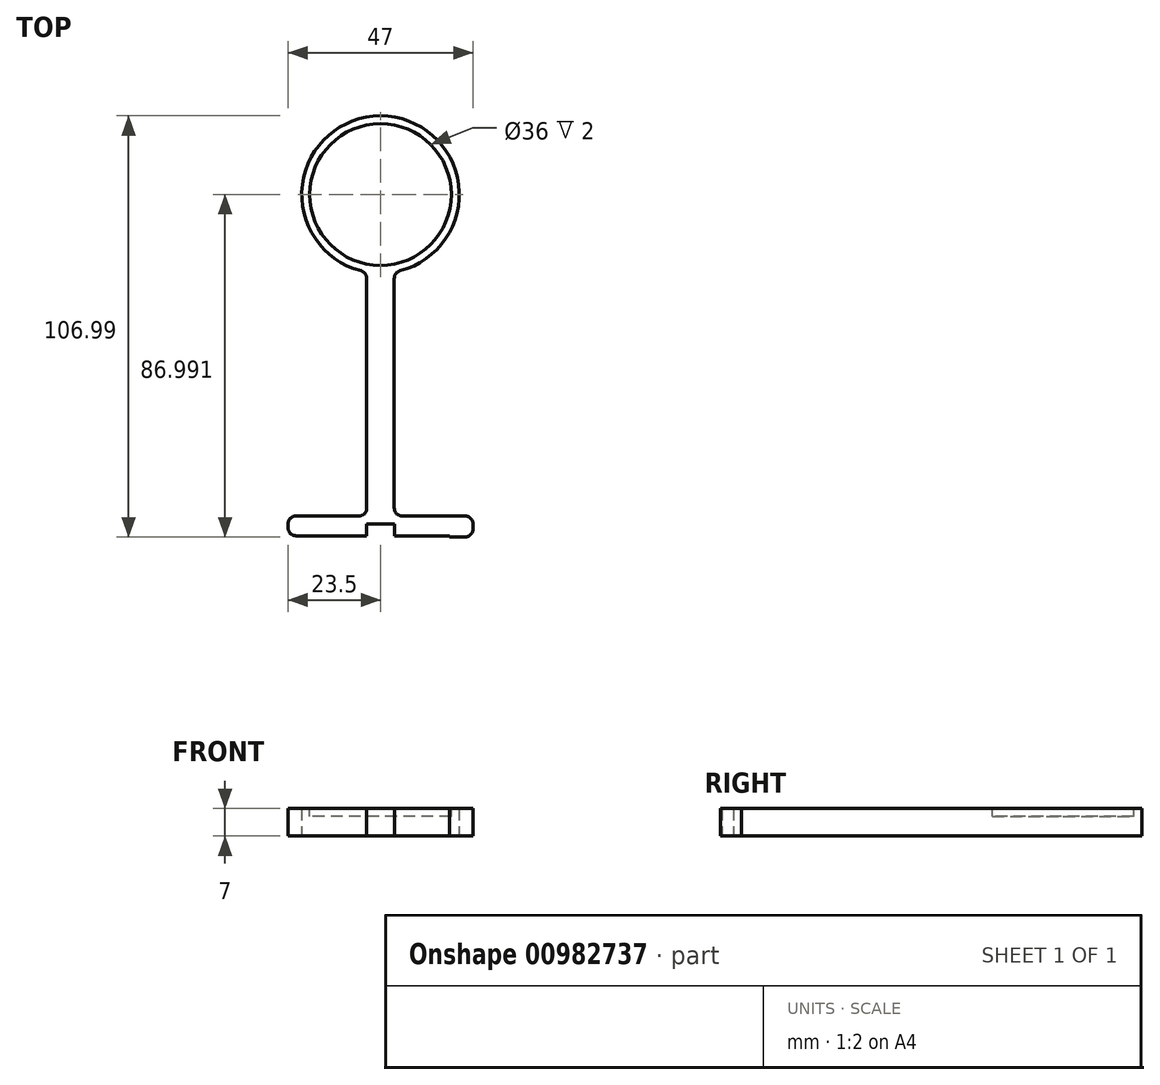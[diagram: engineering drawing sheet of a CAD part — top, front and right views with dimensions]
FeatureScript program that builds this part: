
annotation { "Feature Type Name" : "Feature", "Feature Type Description" : "" }
export const myFeature = defineFeature(function(context is Context, id is Id, definition is map)
    precondition{}
    {
        {
            var Q0;
            Q0=qCreatedBy(makeId("Top.planeOp"),FACE);
            var sketch = newSketch(context, id + "F0", { "sketchPlane" : qUnion([Q0])});
            skLineSegment(sketch, "E0", {"start": v(-3.5, -3) * mm, "end": v(-3.5, -65) * mm});
            skLineSegment(sketch, "E1", {"start": v(-3.5, -65) * mm, "end": v(-23.5, -65) * mm});
            skLineSegment(sketch, "E2", {"start": v(-23.5, -65) * mm, "end": v(-23.5, -70) * mm});
            skLineSegment(sketch, "E3", {"start": v(-23.5, -70) * mm, "end": v(23.5, -70) * mm});
            skLineSegment(sketch, "E4", {"start": v(23.5, -70) * mm, "end": v(23.5, -65) * mm});
            skLineSegment(sketch, "E5", {"start": v(23.5, -65) * mm, "end": v(3.5, -65) * mm});
            skLineSegment(sketch, "E6", {"start": v(3.5, -65) * mm, "end": v(3.5, -3) * mm});
            skLineSegment(sketch, "E7.bottom", {"start": v(3.6, -70) * mm, "end": v(-3.6, -70) * mm});
            skLineSegment(sketch, "E7.top", {"start": v(3.6, -67) * mm, "end": v(-3.6, -67) * mm});
            skLineSegment(sketch, "E7.left", {"start": v(3.6, -70) * mm, "end": v(3.6, -67) * mm});
            skLineSegment(sketch, "E7.right", {"start": v(-3.6, -70) * mm, "end": v(-3.6, -67) * mm});
            skPoint(sketch, "E7.middle", {"position": v(0, -68.5) * mm});
            skCircle(sketch, "E8", {"center": v(0, 16.7) * mm, "radius": 20 * mm});
            skLineSegment(sketch, "E9.bottom", {"start": v(-23.5, -70) * mm, "end": v(-17.5, -70) * mm});
            skLineSegment(sketch, "E9.top", {"start": v(-23.5, -70.3) * mm, "end": v(-17.5, -70.3) * mm});
            skLineSegment(sketch, "E9.left", {"start": v(-23.5, -70) * mm, "end": v(-23.5, -70.3) * mm});
            skLineSegment(sketch, "E9.right", {"start": v(-17.5, -70) * mm, "end": v(-17.5, -70.3) * mm});
            skLineSegment(sketch, "E10.MirrorCS", {"start": v(23.5, -70.3) * mm, "end": v(17.5, -70.3) * mm});
            skLineSegment(sketch, "E11.MirrorCS", {"start": v(23.5, -70) * mm, "end": v(17.5, -70) * mm});
            skLineSegment(sketch, "E12.MirrorCS", {"start": v(23.5, -70) * mm, "end": v(23.5, -70.3) * mm});
            skLineSegment(sketch, "E13.MirrorCS", {"start": v(17.5, -70) * mm, "end": v(17.5, -70.3) * mm});
            skSolve(sketch);
        }
        {
            var Q0;
            Q0=makeQuery(id+"F0.imprint","IMPRINT",FACE,{"disambiguationData":[TD([[makeQuery(id+"F0.imprint","IMPRINT",EDGE,{"derivedFrom":sQuery(id+"F0.wireOp",EDGE,"0U4RxweM-u2bA-2Qqt-OOBg-x1ftkZs6jUrD")}),1.0]])]});
            var Q1;
            {var subQ0=sQuery(id+"F0.wireOp",EDGE,"im0v1Rov-prSM-cwdN-f0IW-ScqFdnQkXUSi");Q1=makeQuery(id+"F0.imprint","IMPRINT",FACE,{"disambiguationData":[TD([[makeQuery(id+"F0.imprint","IMPRINT",EDGE,{"derivedFrom":subQ0}),1.0]])]});}
            var Q2;
            {var subQ7=sQuery(id+"F0.wireOp",EDGE,"E0");Q2=makeQuery(id+"F0.imprint","IMPRINT",FACE,{"disambiguationData":[TD([[makeQuery(id+"F0.imprint","IMPRINT",EDGE,{"derivedFrom":subQ7}),1.0]])]});}
            var Q3;
            {var subQ0=sQuery(id+"F0.wireOp",EDGE,"E8");var subQ1=makeQuery(id+"F0.imprint","INTERSECT",VERTEX,{"derivedFrom":[sQuery(id+"F0.wireOp",EDGE,"E0"),subQ0]});Q3=makeQuery(id+"F0.imprint","IMPRINT",FACE,{"disambiguationData":[TD([[makeQuery(id+"F0.imprint","IMPRINT",EDGE,{"disambiguationData":[TD([[subQ1,-1.0]])],"derivedFrom":subQ0}),1.0]])]});}
            var Q4;
            Q4=makeQuery(id+"F0.imprint","IMPRINT",FACE,{"disambiguationData":[TD([[makeQuery(id+"F0.imprint","IMPRINT",EDGE,{"derivedFrom":sQuery(id+"F0.wireOp",EDGE,"E9.bottom")}),-1.0]])]});
            var Q5;
            Q5=makeQuery(id+"F0.imprint","IMPRINT",FACE,{"disambiguationData":[TD([[makeQuery(id+"F0.imprint","IMPRINT",EDGE,{"derivedFrom":sQuery(id+"F0.wireOp",EDGE,"E10.MirrorCS")}),-1.0]])]});
            extrude(context, id + "F1", {"entities" : qUnion([Q0, Q1, Q2, Q3, Q4, Q5]), "depth" : 7 * mm, "offsetDistance" : 25 * mm});
        }
        {
            var Q0;
            Q0=makeQuery(id+"F1.opExtrude","CAP_FACE",FACE,{"disambiguationData":[OSD([sQuery(id+"F0.wireOp",EDGE,"E0"),sQuery(id+"F0.wireOp",EDGE,"E1"),sQuery(id+"F0.wireOp",EDGE,"E2"),sQuery(id+"F0.wireOp",EDGE,"E3"),sQuery(id+"F0.wireOp",EDGE,"E4"),sQuery(id+"F0.wireOp",EDGE,"E5"),sQuery(id+"F0.wireOp",EDGE,"E6"),sQuery(id+"F0.wireOp",EDGE,"E7.top"),sQuery(id+"F0.wireOp",EDGE,"E7.left"),sQuery(id+"F0.wireOp",EDGE,"E7.right"),sQuery(id+"F0.wireOp",EDGE,"E8")])],"isStart":false});
            var sketch = newSketch(context, id + "F2", { "sketchPlane" : qUnion([Q0])});
            skCircle(sketch, "E14", {"center": v(0, 16.7) * mm, "radius": 18 * mm});
            skSolve(sketch);
        }
        {
            var Q0;
            Q0=makeQuery(id+"F2.imprint","IMPRINT",FACE,{"disambiguationData":[TD([[makeQuery(id+"F2.imprint","IMPRINT",EDGE,{"derivedFrom":sQuery(id+"F2.wireOp",EDGE,"E14")}),1.0]])]});
            extrude(context, id + "F3", {"entities" : qUnion([Q0]), "operationType" : NewBodyOperationType.REMOVE, "oppositeDirection" : true, "depth" : 2 * mm, "offsetDistance" : 25 * mm});
        }
        {
            var Q0;
            Q0=makeQuery(id+"F1.opExtrude","SWEPT_EDGE",EDGE,{"disambiguationData":[OSD([sQuery(id+"F0.wireOp",EDGE,"E0"),sQuery(id+"F0.wireOp",EDGE,"E8")])]});
            var Q1;
            Q1=makeQuery(id+"F1.opExtrude","SWEPT_EDGE",EDGE,{"disambiguationData":[OSD([sQuery(id+"F0.wireOp",EDGE,"E6"),sQuery(id+"F0.wireOp",EDGE,"E8")])]});
            var Q2;
            Q2=makeQuery(id+"F1.opExtrude","SWEPT_EDGE",EDGE,{"disambiguationData":[OSD([sQuery(id+"F0.wireOp",EDGE,"E4"),sQuery(id+"F0.wireOp",EDGE,"E5")])]});
            var Q3;
            Q3=makeQuery(id+"F1.opExtrude","SWEPT_EDGE",EDGE,{"disambiguationData":[OSD([sQuery(id+"F0.wireOp",EDGE,"E1"),sQuery(id+"F0.wireOp",EDGE,"E2")])]});
            var Q4;
            Q4=makeQuery(id+"F1.opExtrude","SWEPT_EDGE",EDGE,{"disambiguationData":[OSD([sQuery(id+"F0.wireOp",EDGE,"E0"),sQuery(id+"F0.wireOp",EDGE,"E1")])]});
            var Q5;
            Q5=makeQuery(id+"F1.opExtrude","SWEPT_EDGE",EDGE,{"disambiguationData":[OSD([sQuery(id+"F0.wireOp",EDGE,"E5"),sQuery(id+"F0.wireOp",EDGE,"E6")])]});
            var Q6;
            Q6=makeQuery(id+"F1.opExtrude","SWEPT_EDGE",EDGE,{"disambiguationData":[OSD([sQuery(id+"F0.wireOp",EDGE,"E9.top"),sQuery(id+"F0.wireOp",EDGE,"E9.left")])]});
            var Q7;
            Q7=makeQuery(id+"F1.opExtrude","SWEPT_EDGE",EDGE,{"disambiguationData":[OSD([sQuery(id+"F0.wireOp",EDGE,"E10.MirrorCS"),sQuery(id+"F0.wireOp",EDGE,"E12.MirrorCS")])]});
            fillet(context, id + "F4", {"entities" : qUnion([Q0, Q1, Q2, Q3, Q4, Q5, Q6, Q7]), "radius" : 2 * mm, "tangentPropagation" : true, "allowEdgeOverflow" : false});
        }
    });
